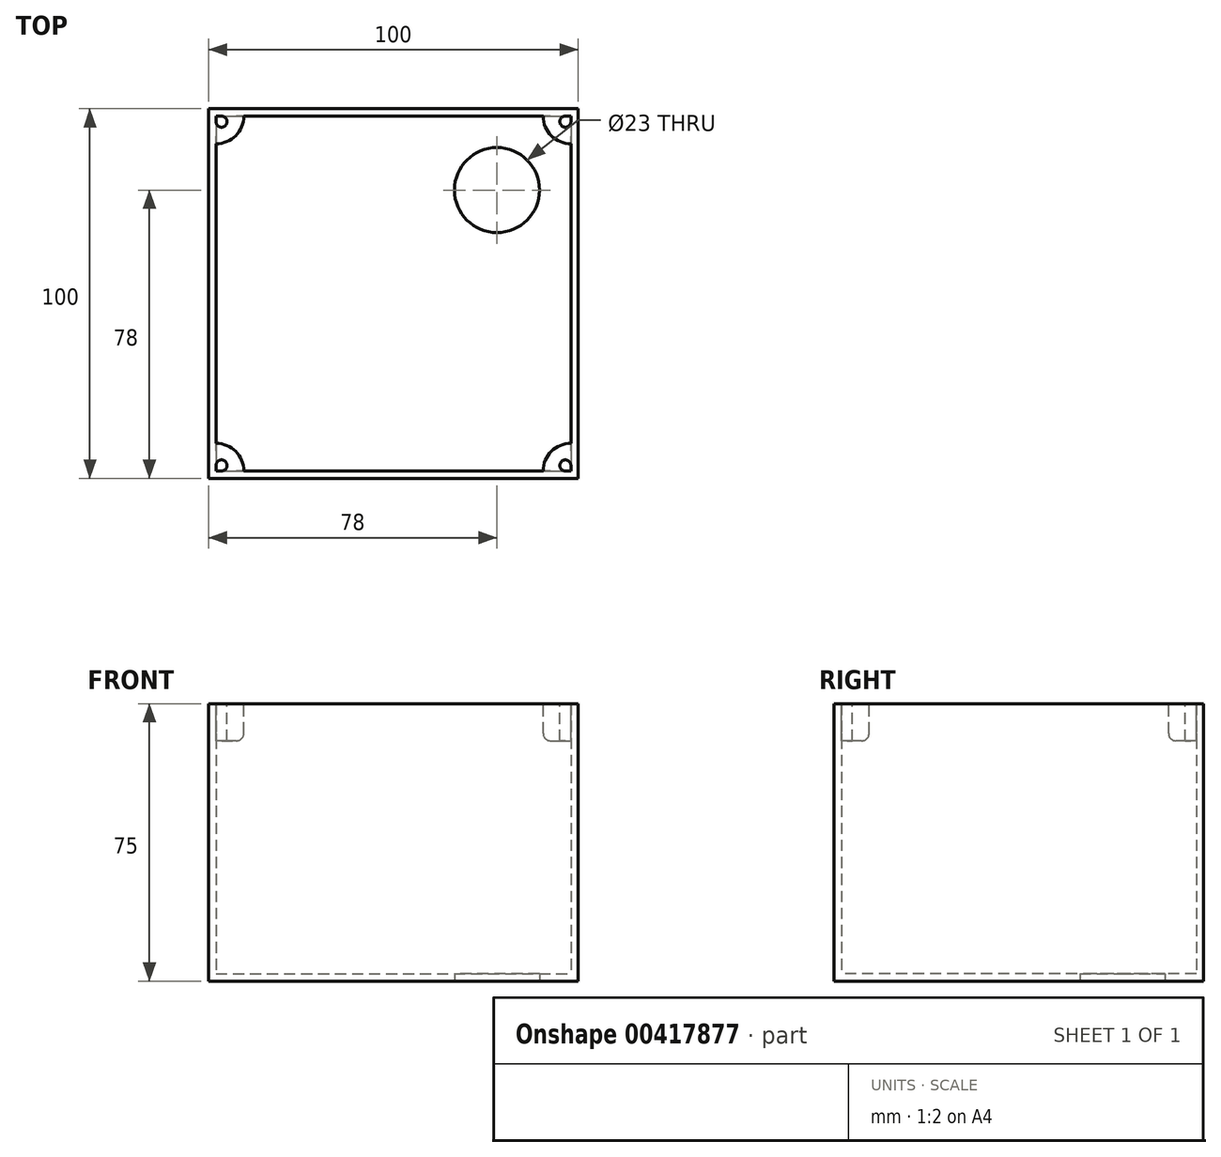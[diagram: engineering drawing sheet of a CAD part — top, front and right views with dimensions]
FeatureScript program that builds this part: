
annotation { "Feature Type Name" : "Feature", "Feature Type Description" : "" }
export const myFeature = defineFeature(function(context is Context, id is Id, definition is map)
    precondition{}
    {
        {
            var Q0;
            Q0=qCreatedBy(makeId("Top.planeOp"),FACE);
            var sketch = newSketch(context, id + "F0", { "sketchPlane" : qUnion([Q0])});
            skLineSegment(sketch, "E0.bottom", {"start": v(-50, 50) * mm, "end": v(50, 50) * mm});
            skLineSegment(sketch, "E0.top", {"start": v(-50, -50) * mm, "end": v(50, -50) * mm});
            skLineSegment(sketch, "E0.left", {"start": v(-50, 50) * mm, "end": v(-50, -50) * mm});
            skLineSegment(sketch, "E0.right", {"start": v(50, 50) * mm, "end": v(50, -50) * mm});
            skPoint(sketch, "E1.middle", {"position": v(28, 28) * mm});
            skLineSegment(sketch, "E2.0", {"start": v(-48, 48) * mm, "end": v(48, 48) * mm});
            skLineSegment(sketch, "E2.1", {"start": v(-48, 48) * mm, "end": v(-48, -48) * mm});
            skLineSegment(sketch, "E2.2", {"start": v(-48, -48) * mm, "end": v(48, -48) * mm});
            skLineSegment(sketch, "E2.3", {"start": v(48, 48) * mm, "end": v(48, -48) * mm});
            skCircle(sketch, "E3", {"center": v(28, 28) * mm, "radius": 11.5 * mm});
            skSolve(sketch);
        }
        {
            var Q0;
            Q0=makeQuery(id+"F0.imprint","IMPRINT",FACE,{"disambiguationData":[TD([[makeQuery(id+"F0.imprint","IMPRINT",EDGE,{"derivedFrom":sQuery(id+"F0.wireOp",EDGE,"E0.bottom")}),-1.0]])]});
            extrude(context, id + "F1", {"entities" : qUnion([Q0]), "depth" : 75 * mm});
        }
        {
            var Q0;
            Q0=makeQuery(id+"F0.imprint","IMPRINT",FACE,{"disambiguationData":[TD([[makeQuery(id+"F0.imprint","IMPRINT",EDGE,{"derivedFrom":sQuery(id+"F0.wireOp",EDGE,"E2.0")}),-1.0]])]});
            extrude(context, id + "F2", {"entities" : qUnion([Q0]), "operationType" : NewBodyOperationType.ADD, "depth" : 2 * mm});
        }
        {
            var Q0;
            Q0=makeQuery(id+"F1.opExtrude","CAP_FACE",FACE,{"disambiguationData":[OSD([sQuery(id+"F0.wireOp",EDGE,"E0.bottom"),sQuery(id+"F0.wireOp",EDGE,"E0.top"),sQuery(id+"F0.wireOp",EDGE,"E0.left"),sQuery(id+"F0.wireOp",EDGE,"E0.right"),sQuery(id+"F0.wireOp",EDGE,"E2.0"),sQuery(id+"F0.wireOp",EDGE,"E2.1"),sQuery(id+"F0.wireOp",EDGE,"E2.2"),sQuery(id+"F0.wireOp",EDGE,"E2.3")])],"isStart":false});
            var sketch = newSketch(context, id + "F3", { "sketchPlane" : qUnion([Q0])});
            skArc(sketch, "E4", {"start": v(40.5, 48) * mm, "mid": v(42.7, 42.7) * mm, "end": v(48, 40.5) * mm});
            skArc(sketch, "E5", {"start": v(48, -40.5) * mm, "mid": v(42.7, -42.7) * mm, "end": v(40.5, -48) * mm});
            skArc(sketch, "E6", {"start": v(-40.5, -48) * mm, "mid": v(-42.7, -42.7) * mm, "end": v(-48, -40.5) * mm});
            skArc(sketch, "E7", {"start": v(-48, 40.5) * mm, "mid": v(-42.7, 42.7) * mm, "end": v(-40.5, 48) * mm});
            skLineSegment(sketch, "E8.bottom", {"start": v(-48, 48) * mm, "end": v(48, 48) * mm});
            skLineSegment(sketch, "E8.top", {"start": v(-48, -48) * mm, "end": v(48, -48) * mm});
            skLineSegment(sketch, "E8.left", {"start": v(-48, 48) * mm, "end": v(-48, -48) * mm});
            skLineSegment(sketch, "E8.right", {"start": v(48, 48) * mm, "end": v(48, -48) * mm});
            skCircle(sketch, "E9", {"center": v(46.5, 46.5) * mm, "radius": 1.5 * mm});
            skCircle(sketch, "E10", {"center": v(46.5, -46.5) * mm, "radius": 1.5 * mm});
            skCircle(sketch, "E11", {"center": v(-46.5, -46.5) * mm, "radius": 1.5 * mm});
            skCircle(sketch, "E12", {"center": v(-46.5, 46.5) * mm, "radius": 1.5 * mm});
            skSolve(sketch);
        }
        {
            var Q0;
            {var subQ0=sQuery(id+"F3.wireOp",EDGE,"E4");Q0=makeQuery(id+"F3.imprint","IMPRINT",FACE,{"disambiguationData":[TD([[makeQuery(id+"F3.imprint","IMPRINT",EDGE,{"derivedFrom":subQ0}),1.0]])]});}
            var Q1;
            {var subQ0=sQuery(id+"F3.wireOp",EDGE,"E5");Q1=makeQuery(id+"F3.imprint","IMPRINT",FACE,{"disambiguationData":[TD([[makeQuery(id+"F3.imprint","IMPRINT",EDGE,{"derivedFrom":subQ0}),1.0]])]});}
            var Q2;
            {var subQ0=sQuery(id+"F3.wireOp",EDGE,"E6");Q2=makeQuery(id+"F3.imprint","IMPRINT",FACE,{"disambiguationData":[TD([[makeQuery(id+"F3.imprint","IMPRINT",EDGE,{"derivedFrom":subQ0}),1.0]])]});}
            var Q3;
            {var subQ0=sQuery(id+"F3.wireOp",EDGE,"E7");Q3=makeQuery(id+"F3.imprint","IMPRINT",FACE,{"disambiguationData":[TD([[makeQuery(id+"F3.imprint","IMPRINT",EDGE,{"derivedFrom":subQ0}),1.0]])]});}
            extrude(context, id + "F4", {"entities" : qUnion([Q0, Q1, Q2, Q3]), "operationType" : NewBodyOperationType.ADD, "depth" : -10 * mm});
        }
        {
            var Q0;
            Q0=makeQuery(id+"F4.opExtrude","CAP_EDGE",EDGE,{"disambiguationData":[OSD([sQuery(id+"F3.wireOp",EDGE,"E6")])],"isStart":false});
            var Q1;
            Q1=makeQuery(id+"F4.opExtrude","CAP_EDGE",EDGE,{"disambiguationData":[OSD([sQuery(id+"F3.wireOp",EDGE,"E7")])],"isStart":false});
            var Q2;
            Q2=makeQuery(id+"F4.opExtrude","CAP_EDGE",EDGE,{"disambiguationData":[OSD([sQuery(id+"F3.wireOp",EDGE,"E4")])],"isStart":false});
            var Q3;
            Q3=makeQuery(id+"F4.opExtrude","CAP_EDGE",EDGE,{"disambiguationData":[OSD([sQuery(id+"F3.wireOp",EDGE,"E5")])],"isStart":false});
            fillet(context, id + "F5", {"entities" : qUnion([Q0, Q1, Q2, Q3]), "radius" : 2 * mm, "tangentPropagation" : true, "allowEdgeOverflow" : false});
        }
        {
            var Q0;
            {var subQ0=sQuery(id+"F3.wireOp",EDGE,"E12");var subQ1=makeQuery(id+"F3.imprint","INTERSECT",VERTEX,{"derivedFrom":[sQuery(id+"F3.wireOp",EDGE,"E8.bottom"),subQ0]});Q0=makeQuery(id+"F3.imprint","IMPRINT",FACE,{"disambiguationData":[TD([[makeQuery(id+"F3.imprint","IMPRINT",EDGE,{"disambiguationData":[TD([[subQ1,-1.0]])],"derivedFrom":subQ0}),1.0]])]});}
            var Q1;
            {var subQ0=sQuery(id+"F3.wireOp",EDGE,"E9");var subQ1=makeQuery(id+"F3.imprint","INTERSECT",VERTEX,{"derivedFrom":[sQuery(id+"F3.wireOp",EDGE,"E8.bottom"),subQ0]});Q1=makeQuery(id+"F3.imprint","IMPRINT",FACE,{"disambiguationData":[TD([[makeQuery(id+"F3.imprint","IMPRINT",EDGE,{"disambiguationData":[TD([[subQ1,1.0]])],"derivedFrom":subQ0}),1.0]])]});}
            var Q2;
            {var subQ0=sQuery(id+"F3.wireOp",EDGE,"E10");var subQ1=makeQuery(id+"F3.imprint","INTERSECT",VERTEX,{"derivedFrom":[sQuery(id+"F3.wireOp",EDGE,"E8.top"),subQ0]});Q2=makeQuery(id+"F3.imprint","IMPRINT",FACE,{"disambiguationData":[TD([[makeQuery(id+"F3.imprint","IMPRINT",EDGE,{"disambiguationData":[TD([[subQ1,1.0]])],"derivedFrom":subQ0}),1.0]])]});}
            var Q3;
            {var subQ0=sQuery(id+"F3.wireOp",EDGE,"E11");var subQ1=makeQuery(id+"F3.imprint","INTERSECT",VERTEX,{"derivedFrom":[sQuery(id+"F3.wireOp",EDGE,"E8.top"),subQ0]});Q3=makeQuery(id+"F3.imprint","IMPRINT",FACE,{"disambiguationData":[TD([[makeQuery(id+"F3.imprint","IMPRINT",EDGE,{"disambiguationData":[TD([[subQ1,1.0]])],"derivedFrom":subQ0}),1.0]])]});}
            extrude(context, id + "F6", {"entities" : qUnion([Q0, Q1, Q2, Q3]), "operationType" : NewBodyOperationType.REMOVE, "oppositeDirection" : true, "depth" : 10 * mm});
        }
    });
